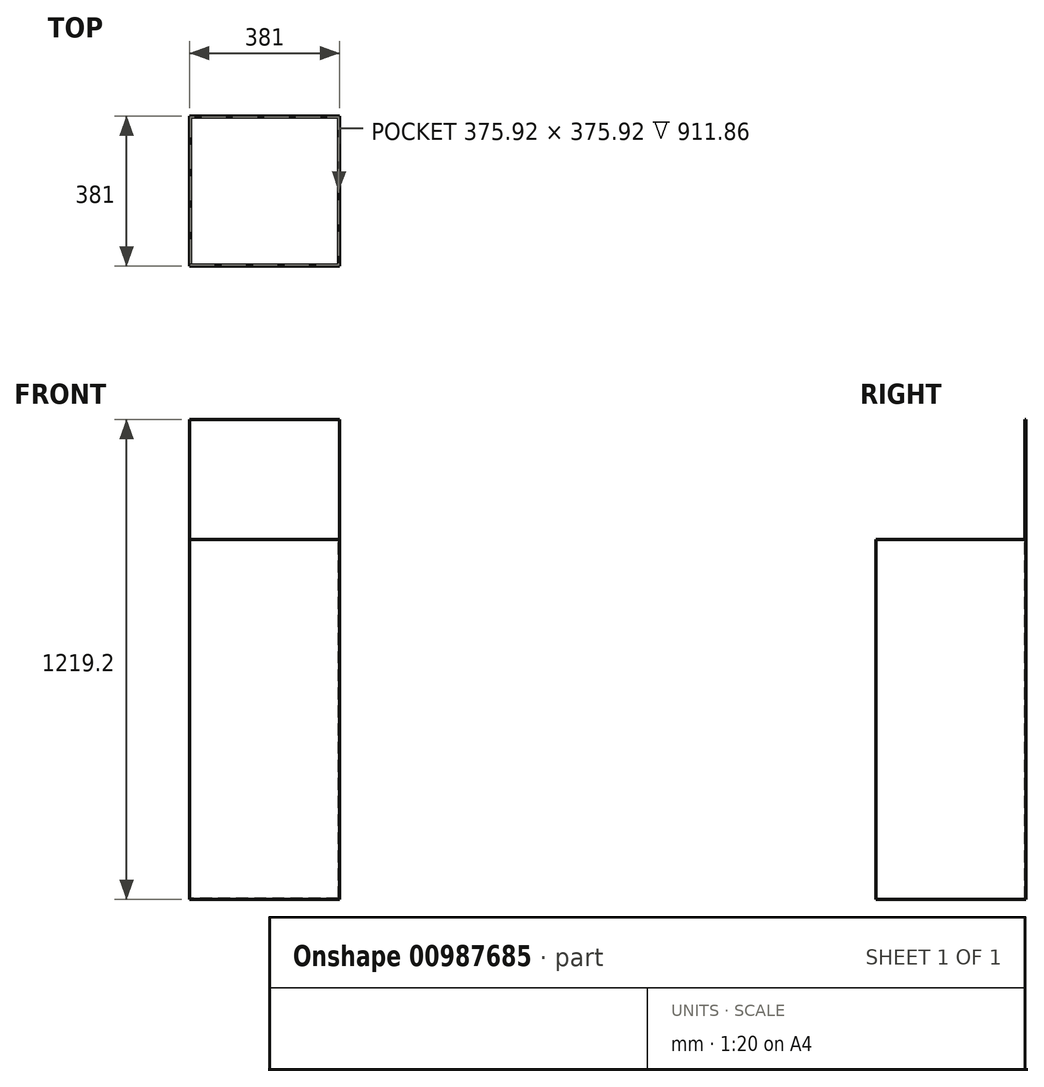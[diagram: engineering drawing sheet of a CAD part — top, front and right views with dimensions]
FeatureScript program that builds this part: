
annotation { "Feature Type Name" : "Feature", "Feature Type Description" : "" }
export const myFeature = defineFeature(function(context is Context, id is Id, definition is map)
    precondition{}
    {
        {
            var Q0;
            Q0=qCreatedBy(makeId("Front.planeOp"),FACE);
            var sketch = newSketch(context, id + "F0", { "sketchPlane" : qUnion([Q0])});
            skLineSegment(sketch, "E0.bottom", {"start": v(190.5, -457.2) * mm, "end": v(-190.5, -457.2) * mm});
            skLineSegment(sketch, "E0.top", {"start": v(190.5, 457.2) * mm, "end": v(-190.5, 457.2) * mm});
            skLineSegment(sketch, "E0.left", {"start": v(190.5, -457.2) * mm, "end": v(190.5, 457.2) * mm});
            skLineSegment(sketch, "E0.right", {"start": v(-190.5, -457.2) * mm, "end": v(-190.5, 457.2) * mm});
            skSolve(sketch);
        }
        {
            var Q0;
            Q0 = qSketchRegion(id + "F0", true);
            extrude(context, id + "F1", {"entities" : qUnion([Q0]), "depth" : 381 * mm, "offsetDistance" : 25.4 * mm, "symmetric" : true});
        }
        {
            var Q0;
            Q0=makeQuery(id+"F1.opExtrude","SWEPT_FACE",FACE,{"disambiguationData":[OSD([sQuery(id+"F0.wireOp",EDGE,"E0.top")])]});
            shell(context, id + "F2", {"entities" : qUnion([Q0]), "thickness" : 2.54 * mm});
        }
        {
            var Q0;
            Q0=makeQuery(id+"F1.opExtrude","SWEPT_FACE",FACE,{"disambiguationData":[OSD([sQuery(id+"F0.wireOp",EDGE,"E0.top")])]});
            var sketch = newSketch(context, id + "F3", { "sketchPlane" : qUnion([Q0])});
            skLineSegment(sketch, "E1.0", {"start": v(190.5, 190.5) * mm, "end": v(-190.5, 190.5) * mm});
            skLineSegment(sketch, "E2", {"start": v(-190.5, 190.5) * mm, "end": v(-190.5, 187.96) * mm});
            skLineSegment(sketch, "E3", {"start": v(190.5, 190.5) * mm, "end": v(190.5, 187.96) * mm});
            skLineSegment(sketch, "E4", {"start": v(190.5, 187.96) * mm, "end": v(-190.5, 187.96) * mm});
            skSolve(sketch);
        }
        {
            var Q0;
            Q0 = qSketchRegion(id + "F3", true);
            extrude(context, id + "F4", {"entities" : qUnion([Q0]), "operationType" : NewBodyOperationType.ADD, "depth" : 304.8 * mm, "offsetDistance" : 25.4 * mm});
        }
    });
